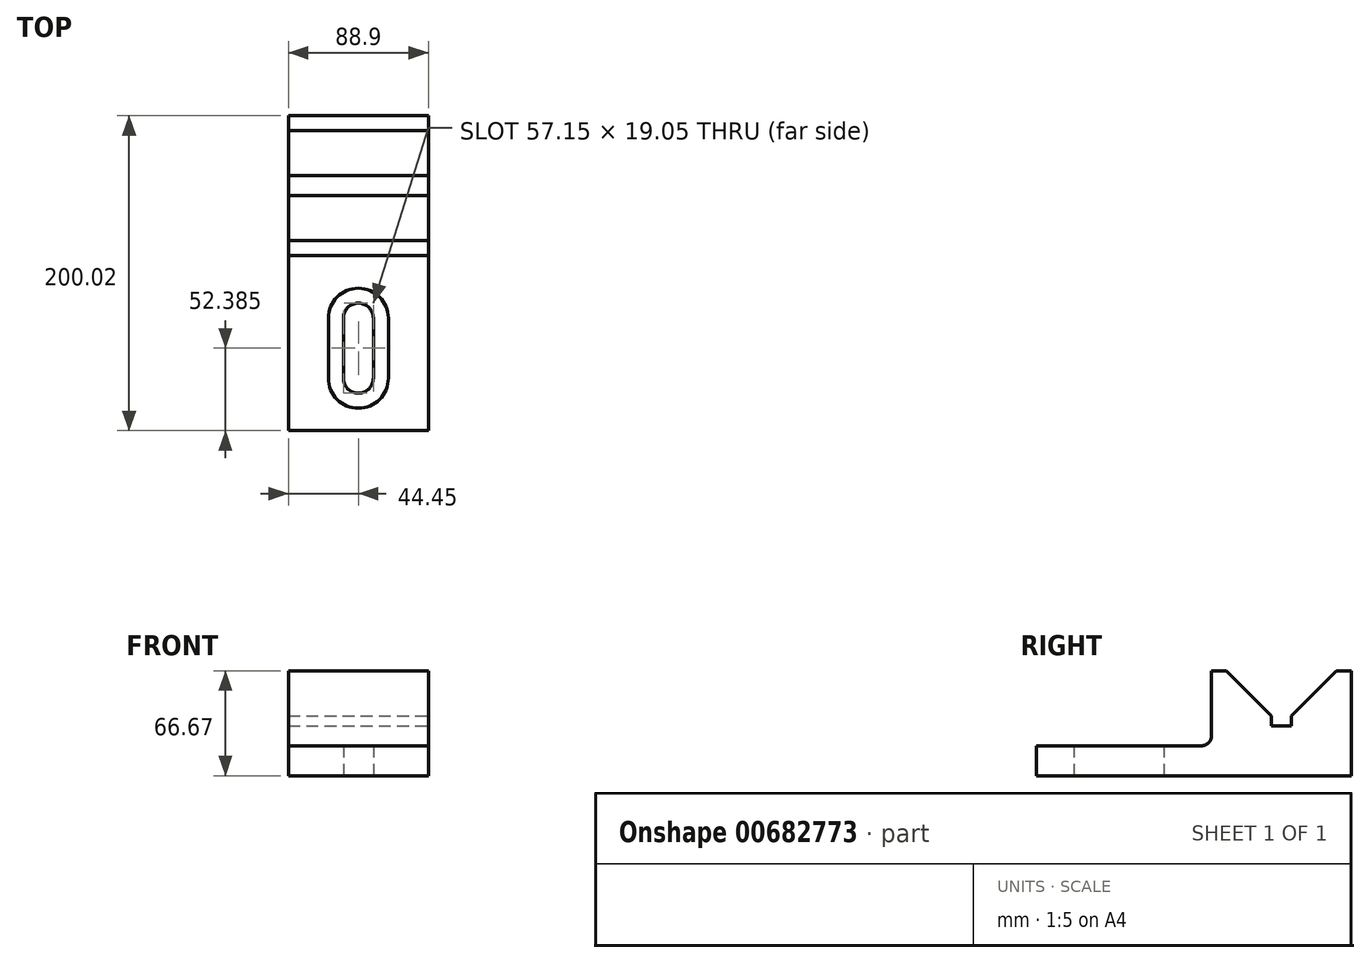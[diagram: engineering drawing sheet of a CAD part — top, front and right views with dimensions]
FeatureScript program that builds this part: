
annotation { "Feature Type Name" : "Feature", "Feature Type Description" : "" }
export const myFeature = defineFeature(function(context is Context, id is Id, definition is map)
    precondition{}
    {
        {
            var Q0;
            Q0=qCreatedBy(makeId("Right.planeOp"),FACE);
            var sketch = newSketch(context, id + "F0", { "sketchPlane" : qUnion([Q0])});
            skLineSegment(sketch, "E0.left", {"start": v(-61.46, 66.68) * mm, "end": v(-61.46, 0) * mm});
            skLineSegment(sketch, "E1.left", {"start": v(-61.46, 0) * mm, "end": v(-61.46, 19.05) * mm});
            skLineSegment(sketch, "E2.MirrorCS", {"start": v(-150.36, 66.68) * mm, "end": v(-140.83, 66.68) * mm});
            skLineSegment(sketch, "E3.MirrorCS", {"start": v(-61.46, 66.68) * mm, "end": v(-70.98, 66.68) * mm});
            skLineSegment(sketch, "E4.MirrorCS", {"start": v(-140.83, 66.68) * mm, "end": v(-150.36, 66.68) * mm});
            skLineSegment(sketch, "E5.MirrorCS", {"start": v(-99.56, 38.1) * mm, "end": v(-99.56, 31.75) * mm});
            skLineSegment(sketch, "E6.MirrorCS", {"start": v(-112.26, 38.1) * mm, "end": v(-112.26, 31.75) * mm});
            skArc(sketch, "E7.MirrorCS", {"start": v(-150.36, 25.4) * mm, "mid": v(-152.22, 20.9) * mm, "end": v(-156.7, 19.05) * mm});
            skLineSegment(sketch, "E8.MirrorCS", {"start": v(-99.56, 31.75) * mm, "end": v(-112.26, 31.75) * mm});
            skLineSegment(sketch, "E9.MirrorCS", {"start": v(-74.16, 0) * mm, "end": v(-72.64, -1.52) * mm});
            skLineSegment(sketch, "E10.MirrorCS", {"start": v(-150.36, 0) * mm, "end": v(-140.83, 0) * mm});
            skLineSegment(sketch, "E11.MirrorCS", {"start": v(-61.46, 0) * mm, "end": v(-150.36, 0) * mm});
            skLineSegment(sketch, "E12.MirrorCS", {"start": v(-150.36, 66.68) * mm, "end": v(-150.36, 25.4) * mm});
            skLineSegment(sketch, "E13.MirrorCS", {"start": v(-61.46, 0) * mm, "end": v(-70.98, 0) * mm});
            skPoint(sketch, "E14.MirrorP", {"position": v(-105.9, 33.34) * mm});
            skPoint(sketch, "E15.MirrorP", {"position": v(-105.9, 31.75) * mm});
            skLineSegment(sketch, "E16.MirrorCS", {"start": v(-261.48, 0) * mm, "end": v(-261.48, 19.05) * mm});
            skLineSegment(sketch, "E17.MirrorCS", {"start": v(-156.7, 19.05) * mm, "end": v(-261.48, 19.05) * mm});
            skLineSegment(sketch, "E18.MirrorCS", {"start": v(-140.83, 66.68) * mm, "end": v(-112.26, 38.1) * mm});
            skPoint(sketch, "E19.MirrorP", {"position": v(-105.9, 66.68) * mm});
            skLineSegment(sketch, "E20.MirrorCS", {"start": v(-61.46, 0) * mm, "end": v(-261.48, 0) * mm});
            skLineSegment(sketch, "E21.MirrorCS", {"start": v(-70.98, 66.68) * mm, "end": v(-99.56, 38.1) * mm});
            skPoint(sketch, "E22.MirrorP", {"position": v(-105.9, 0) * mm});
            skPoint(sketch, "E23.orphan", {"position": v(138.57, 0) * mm});
            skPoint(sketch, "E24.orphan", {"position": v(27.44, 0) * mm});
            skPoint(sketch, "E0.bottom.end.orphan", {"position": v(-51.93, 66.68) * mm});
            skPoint(sketch, "E0.top.end.orphan", {"position": v(-51.93, 0) * mm});
            skSolve(sketch);
        }
        {
            var Q0;
            Q0 = qSketchRegion(id + "F0", true);
            extrude(context, id + "F1", {"entities" : qUnion([Q0]), "oppositeDirection" : true, "depth" : 88.9 * mm, "offsetDistance" : 25.4 * mm});
        }
        {
            var Q0;
            Q0=makeQuery(id+"F1.opExtrude","SWEPT_FACE",FACE,{"disambiguationData":[OSD([sQuery(id+"F0.wireOp",EDGE,"E17.MirrorCS")])]});
            var sketch = newSketch(context, id + "F2", { "sketchPlane" : qUnion([Q0])});
            skArc(sketch, "E25", {"start": v(-25.4, -190.05) * mm, "mid": v(-44.45, -171) * mm, "end": v(-63.5, -190.05) * mm});
            skArc(sketch, "E26", {"start": v(-63.5, -228.15) * mm, "mid": v(-44.45, -247.2) * mm, "end": v(-25.4, -228.15) * mm});
            skArc(sketch, "E27", {"start": v(-53.98, -228.15) * mm, "mid": v(-44.45, -237.67) * mm, "end": v(-34.93, -228.15) * mm});
            skArc(sketch, "E28", {"start": v(-34.93, -190.05) * mm, "mid": v(-44.45, -180.52) * mm, "end": v(-53.98, -190.05) * mm});
            skLineSegment(sketch, "E29", {"start": v(-44.45, -156.7) * mm, "end": v(-63.5, -156.7) * mm});
            skLineSegment(sketch, "E30", {"start": v(-63.5, -190.05) * mm, "end": v(-63.5, -228.15) * mm});
            skLineSegment(sketch, "E31", {"start": v(-63.5, -261.48) * mm, "end": v(-25.4, -261.48) * mm});
            skLineSegment(sketch, "E32", {"start": v(-25.4, -228.15) * mm, "end": v(-25.4, -190.05) * mm});
            skLineSegment(sketch, "E33", {"start": v(-53.98, -190.05) * mm, "end": v(-53.98, -228.15) * mm});
            skLineSegment(sketch, "E34", {"start": v(-34.93, -228.15) * mm, "end": v(-34.93, -190.05) * mm});
            skPoint(sketch, "E35.orphan", {"position": v(-25.4, -156.7) * mm});
            skPoint(sketch, "E36.start.orphan", {"position": v(-44.45, -261.48) * mm});
            skSolve(sketch);
        }
        {
            var Q0;
            Q0 = qSketchRegion(id + "F2", true);
            extrude(context, id + "F3", {"entities" : qUnion([Q0]), "operationType" : NewBodyOperationType.ADD, "depth" : 1 / 101.6 * mm, "offsetDistance" : 25.4 * mm});
        }
        {
            var Q0;
            Q0=makeQuery(id+"F3.boolean.opBoolean","SPLIT",FACE,{"disambiguationData":[TD([makeQuery(id+"F3.opExtrude","SWEPT_FACE",FACE,{"disambiguationData":[OSD([sQuery(id+"F2.wireOp",EDGE,"E27")])]})])],"derivedFrom":makeQuery(id+"F1.opExtrude","SWEPT_FACE",FACE,{"disambiguationData":[OSD([sQuery(id+"F0.wireOp",EDGE,"E17.MirrorCS")])]})});
            extrude(context, id + "F4", {"entities" : qUnion([Q0]), "operationType" : NewBodyOperationType.REMOVE, "oppositeDirection" : true, "depth" : 19.05 * mm, "offsetDistance" : 25.4 * mm});
        }
        {
            var Q0;
            Q0=makeQuery(id+"F3.opExtrude","CAP_EDGE",EDGE,{"disambiguationData":[OSD([sQuery(id+"F2.wireOp",EDGE,"E30")])],"isStart":true});
            fillet(context, id + "F5", {"entities" : qUnion([Q0]), "radius" : 3.17 * mm, "tangentPropagation" : true, "allowEdgeOverflow" : false});
        }
    });
